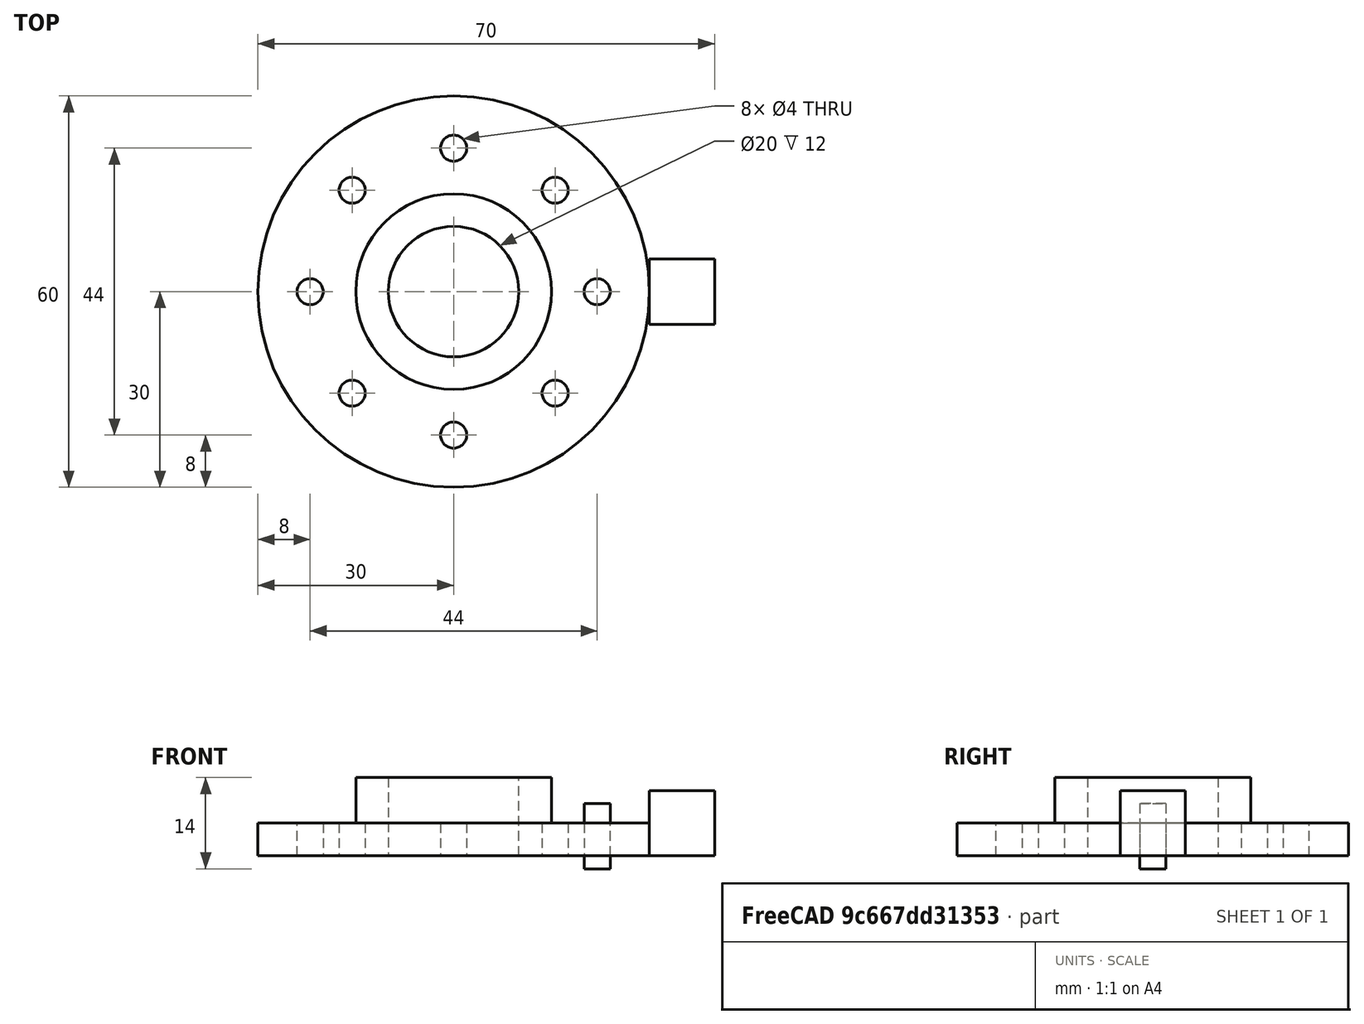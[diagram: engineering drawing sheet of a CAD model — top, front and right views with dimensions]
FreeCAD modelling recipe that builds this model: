
FCSTD DOCUMENT  (FreeCAD 1.0R39285 (Git))
Label: ojt1_t11p01_flange
License: All rights reserved
objects: Part::Cylinder×4, Part::FeaturePython×2, Part::Cut×2, Part::Box×1, Part::MultiFuse×1
note: 8 computed .brp shape members not serialized (recipe doc carries the construction recipe); baked Part::Feature solids carry a one-line shape summary decoded from their .brp

FEATURE [Part::Box] Box  label="Cub"
  AttacherType = Attacher::AttachEngine3D
  Height = 10
  Length = 10
  Placement = pos=(30,-5,0) rot=(0,0,1;0rad)
  Width = 10
FEATURE [Part::FeaturePython] Array  label="Array_tutorial"  # Draft array (typed FeaturePython)
  AlwaysSyncPlacement = false
  Angle = 360
  ArrayType = 1
  Axis = (0,0,1)
  Base = -> Box
  Center = (0,0,0)
  Count = 6
  ExpandArray = false
  Fuse = false
  IntervalAxis = (0,0,0)
  IntervalX = (50,0,0)
  IntervalY = (0,50,0)
  IntervalZ = (0,0,50)
  NumberCircles = 3
  NumberPolar = 6
  NumberX = 2
  NumberY = 2
  NumberZ = 1
  PlacementList = 6 placements: [(30,-5,0),(19.3301,23.4808,0),(-10.6699,28.4808,0),(-30,5,0),(-19.3301,-23.4808,0),(10.6699,-28.4808,0)]
  RadialDistance = 50
  ScaleList = (6) [(1,1,1),(1,1,1),(1,1,1),(1,1,1),(1,1,1),(1,1,1)]
  Symmetry = 1
  TangentialDistance = 25
FEATURE [Part::Cylinder] Cylinder  label="basis"
  Angle = 360
  AttacherType = Attacher::AttachEngine3D
  FirstAngle = 0
  Height = 5
  Radius = 30
  SecondAngle = 0
FEATURE [Part::Cylinder] Cylinder001  label="Cilindre"
  Angle = 360
  AttacherType = Attacher::AttachEngine3D
  FirstAngle = 0
  Height = 12
  Radius = 15
  SecondAngle = 0
FEATURE [Part::MultiFuse] Fusion
  Refine = true
  Shapes = -> [Cylinder001,Cylinder]
FEATURE [Part::Cylinder] Cylinder002  label="int"
  Angle = 360
  AttacherType = Attacher::AttachEngine3D
  FirstAngle = 0
  Height = 30
  Placement = pos=(0,0,-2) rot=(0,0,1;0rad)
  Radius = 10
  SecondAngle = 0
FEATURE [Part::Cut] Cut
  Base = -> Fusion
  Refine = true
  Tool = -> Cylinder002
FEATURE [Part::Cylinder] Cylinder003  label="drill"
  Angle = 360
  AttacherType = Attacher::AttachEngine3D
  FirstAngle = 0
  Height = 10
  Placement = pos=(22,0,-2) rot=(0,0,1;0rad)
  Radius = 2
  SecondAngle = 0
FEATURE [Part::FeaturePython] Array001  # Draft array (typed FeaturePython)
  AlwaysSyncPlacement = false
  Angle = 360
  ArrayType = 1
  Axis = (0,0,1)
  Base = -> Cylinder003
  Center = (0,0,1)
  Count = 8
  ExpandArray = false
  Fuse = false
  IntervalAxis = (0,0,0)
  IntervalX = (50,0,0)
  IntervalY = (0,50,0)
  IntervalZ = (0,0,50)
  NumberCircles = 3
  NumberPolar = 8
  NumberX = 2
  NumberY = 2
  NumberZ = 1
  PlacementList = 8 placements: [(22,0,-2),(15.5563,15.5563,-2),(0,22,-2),(-15.5563,15.5563,-2),(-22,2.69422e-15,-2),(-15.5563,-15.5563,-2),(-4.88498e-15,-22,-2),(15.5563,-15.5563,-2)]
  RadialDistance = 50
  ScaleList = (8) [(1,1,1),(1,1,1),(1,1,1),(1,1,1),(1,1,1),(1,1,1),(1,1,1),(1,1,1)]
  Symmetry = 1
  TangentialDistance = 25
FEATURE [Part::Cut] Cut001  label="flange"
  Base = -> Cut
  Refine = true
  Tool = -> Array001
